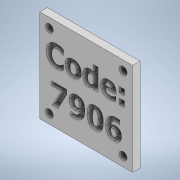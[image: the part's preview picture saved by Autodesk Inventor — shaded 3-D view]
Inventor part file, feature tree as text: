
AUTODESK INVENTOR PART (.ipt)
format: ipt  version: 2021.2 (Build 252289000, 289)  size: 363,008 bytes
history: native  units: in
note: dims shown in document units (in); Inventor stores cm internally (conversion verified against a paired STEP export)
features: sketch x3, extrude x2, hole x1
ambient origin geometry x8: Origin, YZ Plane, XZ Plane, XY Plane, X Axis, Y Axis, Z Axis, Center Point
bodies: Body1 (feature_tree)
feature tree (6):
  extrude  "Extrusion2"  Depth=3.141in
  hole  "Hole1"  [1 undecoded]
  extrude  "Extrusion3"  Depth=2.5in
  sketch  "Sketch2"  dims[d6=3.141in d7=3.141in]
  sketch  "Sketch3"  dims[d8=0.25in d9=0.0in]
  sketch  "Sketch4"  dims[d10=2.5in d11=2.5in d12=0.266in d13=0.75in d14=0.438in d15=0.25in d16=0.5635in d17=1.0in d18=0.8108in d19=2.25in d20=2.25in d21=0.1667in d22=0.0in]
note: 1 required parameter value undecoded (feature->parameter linkage not recoverable at this tier; creation-order binding heuristic only, values carry confidence <= 0.55)
